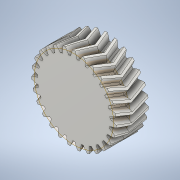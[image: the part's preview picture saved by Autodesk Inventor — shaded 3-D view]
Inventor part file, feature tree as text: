
AUTODESK INVENTOR PART (.ipt)
format: ipt  version: 2020 (Build 240168000, 168)  size: 732,672 bytes
history: native  units: mm (DEFAULTED — no unit token found)
features: other x4, plane x3, extrude x2, sketch x2, mirror x1
ambient origin geometry x8: Origin, YZ Plane, XZ Plane, XY Plane, X Axis, Y Axis, Z Axis, Center Point
bodies: Solid1 (feature_tree)
feature tree (12):
  extrude  "Extrusion1"  Depth=5.0mm TaperAngle=0.0deg
  plane  "Work Plane2"
  plane  "Work Plane8"
  plane  "Work Plane9"
  other  "Spur Gear"
  mirror  "Mirror1"
  sketch  "Sketch1"  dims[d0=26.262248mm d1=5.0mm d2=0.0mm]
  sketch  "Sketch2"  dims[d3=24.545455mm d4=10.0mm d5=0.0mm d16=25.0mm d17=0.0mm d34=1.163553mm d39=0.0mm d41=0.0mm d43=25.0mm d46=25.0mm d47=0.0mm d48=0.0mm]
  other  "Srf1"
  other  "Srf2"
  other  "Pitch Diameter"
  extrude  "ExtrusionSrf2"  Depth=10.0mm TaperAngle=0.0deg
